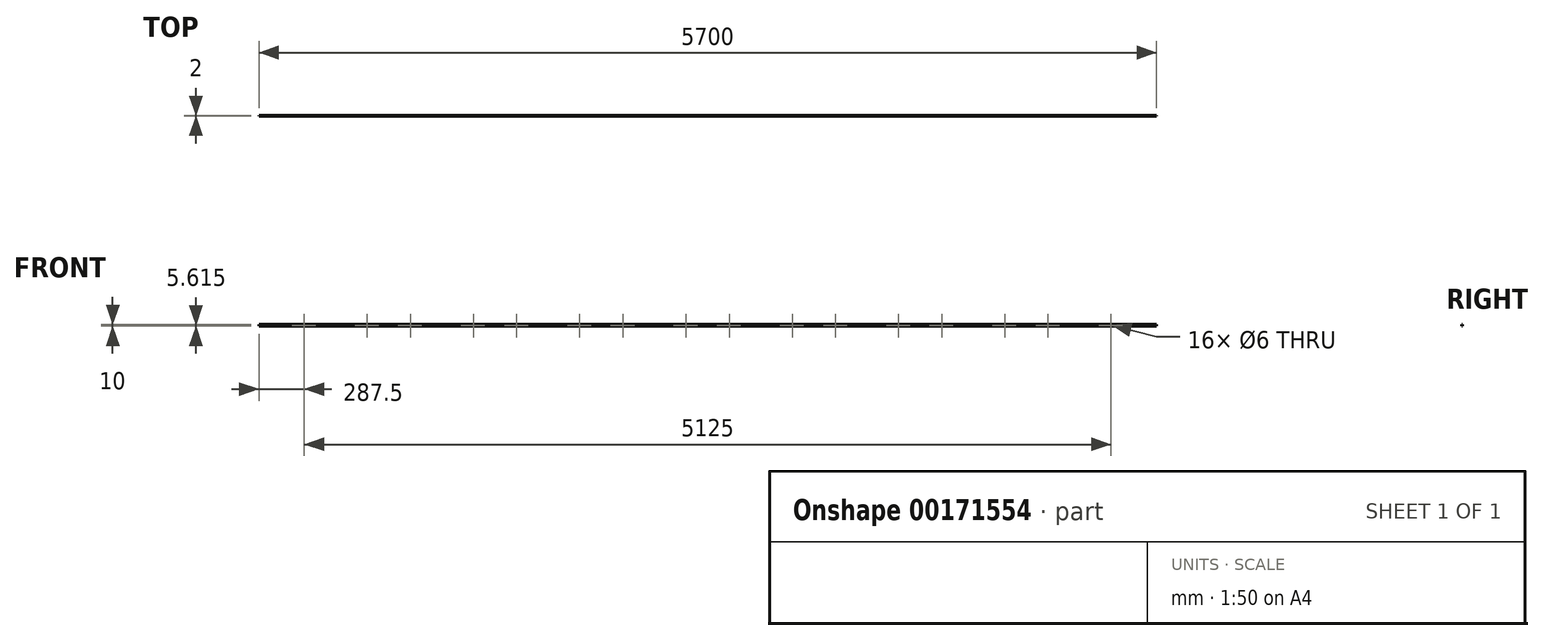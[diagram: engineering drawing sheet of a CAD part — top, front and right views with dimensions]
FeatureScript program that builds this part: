
annotation { "Feature Type Name" : "Feature", "Feature Type Description" : "" }
export const myFeature = defineFeature(function(context is Context, id is Id, definition is map)
    precondition{}
    {
        {
            var Q0;
            Q0=qCreatedBy(makeId("Front.planeOp"),FACE);
            var sketch = newSketch(context, id + "F0", { "sketchPlane" : qUnion([Q0])});
            skLineSegment(sketch, "E0.bottom", {"start": v(0, 0) * mm, "end": v(5700, 0) * mm});
            skLineSegment(sketch, "E0.top", {"start": v(0, 10) * mm, "end": v(5700, 10) * mm});
            skLineSegment(sketch, "E0.left", {"start": v(0, 0) * mm, "end": v(0, 10) * mm});
            skLineSegment(sketch, "E0.right", {"start": v(5700, 0) * mm, "end": v(5700, 10) * mm});
            skSolve(sketch);
        }
        {
            var Q0;
            Q0 = qSketchRegion(id + "F0", true);
            extrude(context, id + "F1", {"entities" : qUnion([Q0]), "depth" : 2 * mm});
        }
        {
            var Q0;
            Q0=makeQuery(id+"F1.opExtrude","CAP_FACE",FACE,{"disambiguationData":[OSD([sQuery(id+"F0.wireOp",EDGE,"E0.bottom"),sQuery(id+"F0.wireOp",EDGE,"E0.top"),sQuery(id+"F0.wireOp",EDGE,"E0.left"),sQuery(id+"F0.wireOp",EDGE,"E0.right")])],"isStart":false});
            var sketch = newSketch(context, id + "F2", { "sketchPlane" : qUnion([Q0])});
            skCircle(sketch, "E1", {"center": v(287.5, 5.61) * mm, "radius": 3 * mm});
            skCircle(sketch, "E2", {"center": v(687.5, 5.61) * mm, "radius": 3 * mm});
            skCircle(sketch, "E3.1.0.0", {"center": v(962.5, 5.61) * mm, "radius": 3 * mm});
            skCircle(sketch, "E3.1.0.1", {"center": v(1362.5, 5.61) * mm, "radius": 3 * mm});
            skCircle(sketch, "E3.2.0.0", {"center": v(1637.5, 5.61) * mm, "radius": 3 * mm});
            skCircle(sketch, "E3.2.0.1", {"center": v(2037.5, 5.61) * mm, "radius": 3 * mm});
            skCircle(sketch, "E3.3.0.0", {"center": v(2312.5, 5.61) * mm, "radius": 3 * mm});
            skCircle(sketch, "E3.3.0.1", {"center": v(2712.5, 5.61) * mm, "radius": 3 * mm});
            skCircle(sketch, "E3.4.0.0", {"center": v(2987.5, 5.61) * mm, "radius": 3 * mm});
            skCircle(sketch, "E3.4.0.1", {"center": v(3387.5, 5.61) * mm, "radius": 3 * mm});
            skCircle(sketch, "E3.5.0.0", {"center": v(3662.5, 5.61) * mm, "radius": 3 * mm});
            skCircle(sketch, "E3.5.0.1", {"center": v(4062.5, 5.61) * mm, "radius": 3 * mm});
            skCircle(sketch, "E3.6.0.0", {"center": v(4337.5, 5.61) * mm, "radius": 3 * mm});
            skCircle(sketch, "E3.6.0.1", {"center": v(4737.5, 5.61) * mm, "radius": 3 * mm});
            skCircle(sketch, "E3.7.0.0", {"center": v(5012.5, 5.61) * mm, "radius": 3 * mm});
            skCircle(sketch, "E3.7.0.1", {"center": v(5412.5, 5.61) * mm, "radius": 3 * mm});
            skLineSegment(sketch, "E3.direction1", {"start": v(287.5, 5.61) * mm, "end": v(962.5, 5.61) * mm, "construction": true});
            skSolve(sketch);
        }
        {
            var Q0;
            Q0 = qSketchRegion(id + "F2", true);
            extrude(context, id + "F3", {"entities" : qUnion([Q0]), "operationType" : NewBodyOperationType.REMOVE, "oppositeDirection" : true, "depth" : 25 * mm});
        }
    });
